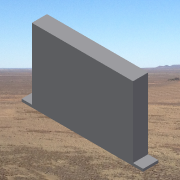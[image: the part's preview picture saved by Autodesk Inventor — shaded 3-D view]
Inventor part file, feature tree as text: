
AUTODESK INVENTOR PART (.ipt)
format: ipt  version: 2014 SP1 (Build 180222100, 222)  size: 112,640 bytes
history: native  units: in
note: dims shown in document units (in); Inventor stores cm internally (conversion verified against a paired STEP export)
features: extrude x1, sketch x1
ambient origin geometry x8: Origin, YZ Plane, XZ Plane, XY Plane, X Axis, Y Axis, Z Axis, Center Point
bodies: Solid1 (feature_tree)
feature tree (2):
  extrude  "Extrusion1"  Depth=0.25in
  sketch  "Sketch1"  dims[d0=12.0in d1=0.25in d2=1.0in d3=7.0in d4=1.5in d5=0.0in]
